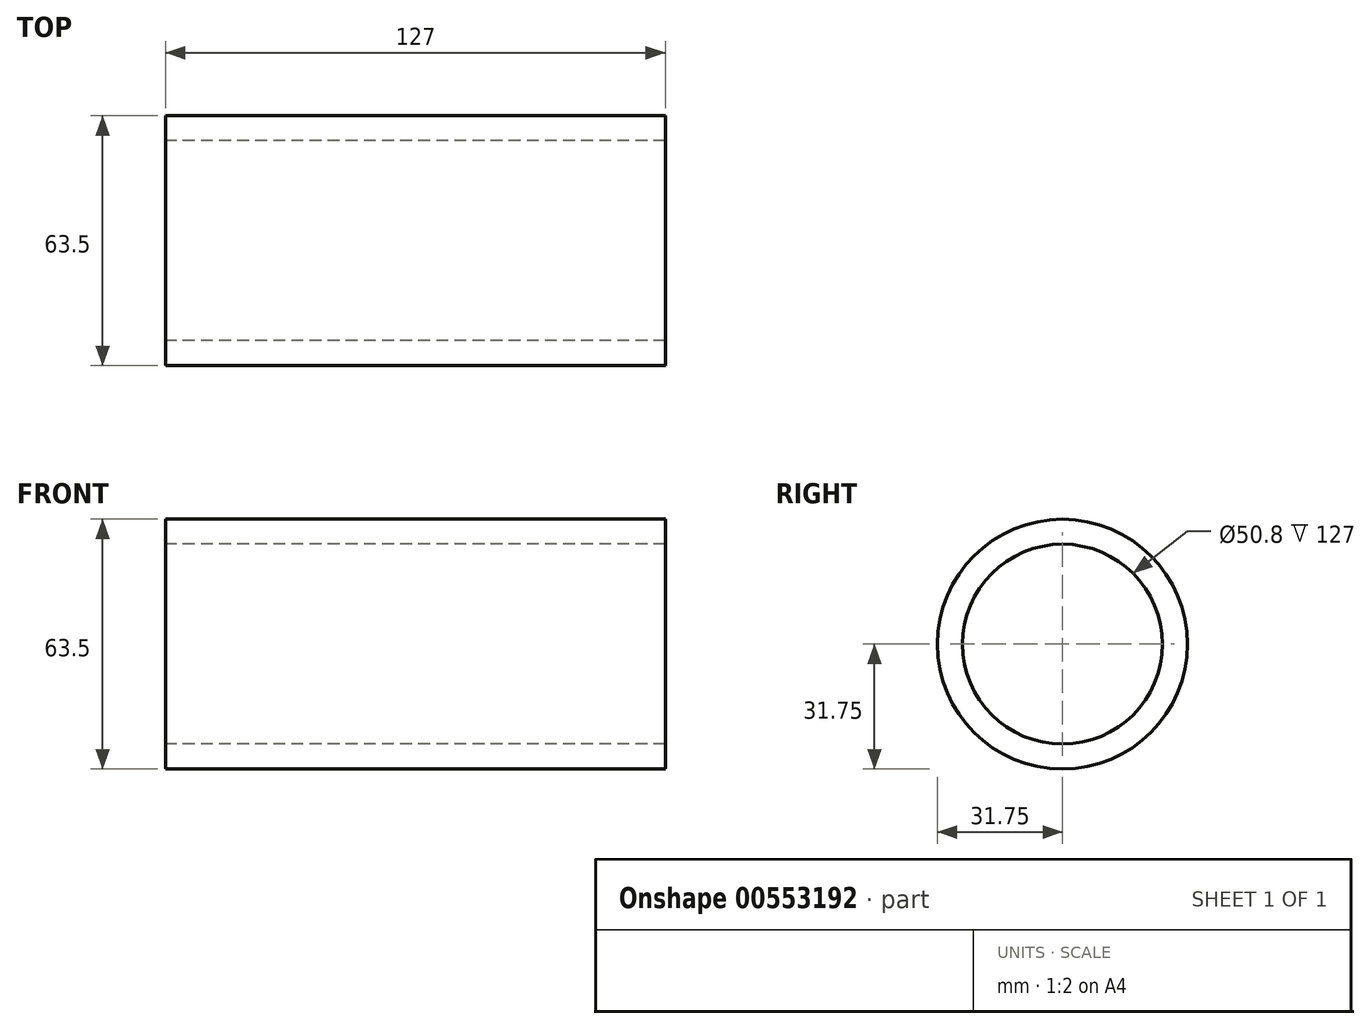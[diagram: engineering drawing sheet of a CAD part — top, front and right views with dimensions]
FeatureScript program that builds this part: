
annotation { "Feature Type Name" : "Feature", "Feature Type Description" : "" }
export const myFeature = defineFeature(function(context is Context, id is Id, definition is map)
    precondition{}
    {
        {
            var Q0;
            Q0=qCreatedBy(makeId("Right.planeOp"),FACE);
            var sketch = newSketch(context, id + "F0", { "sketchPlane" : qUnion([Q0])});
            skCircle(sketch, "E0", {"center": v(0, 0) * mm, "radius": 31.75 * mm});
            skCircle(sketch, "E1", {"center": v(0, 0) * mm, "radius": 25.4 * mm});
            skSolve(sketch);
        }
        {
            var Q0;
            Q0 = qSketchRegion(id + "F0", true);
            extrude(context, id + "F1", {"entities" : qUnion([Q0]), "depth" : 127 * mm, "offsetDistance" : 25.4 * mm});
        }
    });
